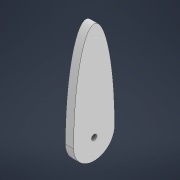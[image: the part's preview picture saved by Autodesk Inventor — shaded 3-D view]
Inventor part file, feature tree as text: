
AUTODESK INVENTOR PART (.ipt)
format: ipt  version: 2022 (Build 260153000, 153)  size: 98,816 bytes
history: native  units: mm
features: extrude x2, sketch x2
ambient origin geometry x8: Origin, YZ Plane, XZ Plane, XY Plane, X Axis, Y Axis, Z Axis, Center Point
bodies: Solid1 (feature_tree)
feature tree (4):
  extrude  "Extrusion1"  Depth=25.0mm
  extrude  "Extrusion4"  Depth=10.0mm TaperAngle=0.0deg
  sketch  "Sketch1"  dims[d0=120.0mm d1=25.0mm]
  sketch  "Sketch4"  dims[d2=50.0mm d3=10.0mm d4=0.0mm d11=6.35mm d12=0.0mm d13=0.0mm]
